# Revit family: Lighting_Floor_Nordlux_Darci-Wall
name_source: partatom
category: Lighting Fixtures
revit_build: Autodesk Revit 2018 (Build: 20170223_1515(x64)
units: mm (PartAtom-declared; Revit-internal decimal feet)

## family parameters
Cut with Voids When Loaded = No
Host = Face
Light Source = No
OmniClass Number = 23.35.47.11
OmniClass Title = Lighting Fixtures
Part Type = Normal
Room Calculation Point = No
Round Connector Dimension = Use Diameter
Shared = No

## types (1)
- ART - (2120551003)
    Apparent Load = 7 VA
    BIMobject category = Wall Mounted
    Beam angle = 121.80°
    Body material = Nordlux - Metal - Black
    CQS = 80.7
    CRI / Ra = 80.3
    Default Elevation = 1219 mm
    Description = With a cool and industrial design, the Darci series by Bjørn + Balle is both a highly functional and aesthetic addition to your home.
    Design country = Denmark
    EANNumber = 2120551003
    Edition number = 1
    Flicker frequency = 100 Hz
    IFC Classification = Light Fixture
    Installation instructions = https://asset.productmarketingcloud.com
    Light bulb material = Nordlux - Glass - Glass transparent
    Light buld thread material = Nordlux - Metal - Black
    Manufacturer = Nordlux
    Manufacturer country = China
    Manufacturer name = Nordlux
    Material main = Metal
    Material secondary = Plastic
    Model = Darci Wall
    NominalVoltage = 230 V
    OmniClass Code = 23-35 47 11
    OmniClass Description = Lighting Fixtures
    Peak [cd] = 109
    Power factor = 0.53
    Product Guid = 6ef90aaa-20ba-4fee-8750-4a3bead90add
    Product SKU = Darci-Wall
    Product data url = https://bimobject.com
    Product family = Lighting
    Product group = Wall
    Product name = Darci Wall
    Product url = https://nordlux.com
    QR code = https://bimobject.com
    Shade inner material = Nordlux - Metal - White RAL 9016
    Shade material = Nordlux - Metal - Black
    TM30 Rf = 83.3
    TM30 Rg = 91.4
    URL = www.nordlux.com
    Weight Net (Kg) = 0,92
    Youtube clip = https://www.youtube.com

## geometry (parser evidence)
native form markers: Sweep x7
no freeform markers — native parametric forms only
